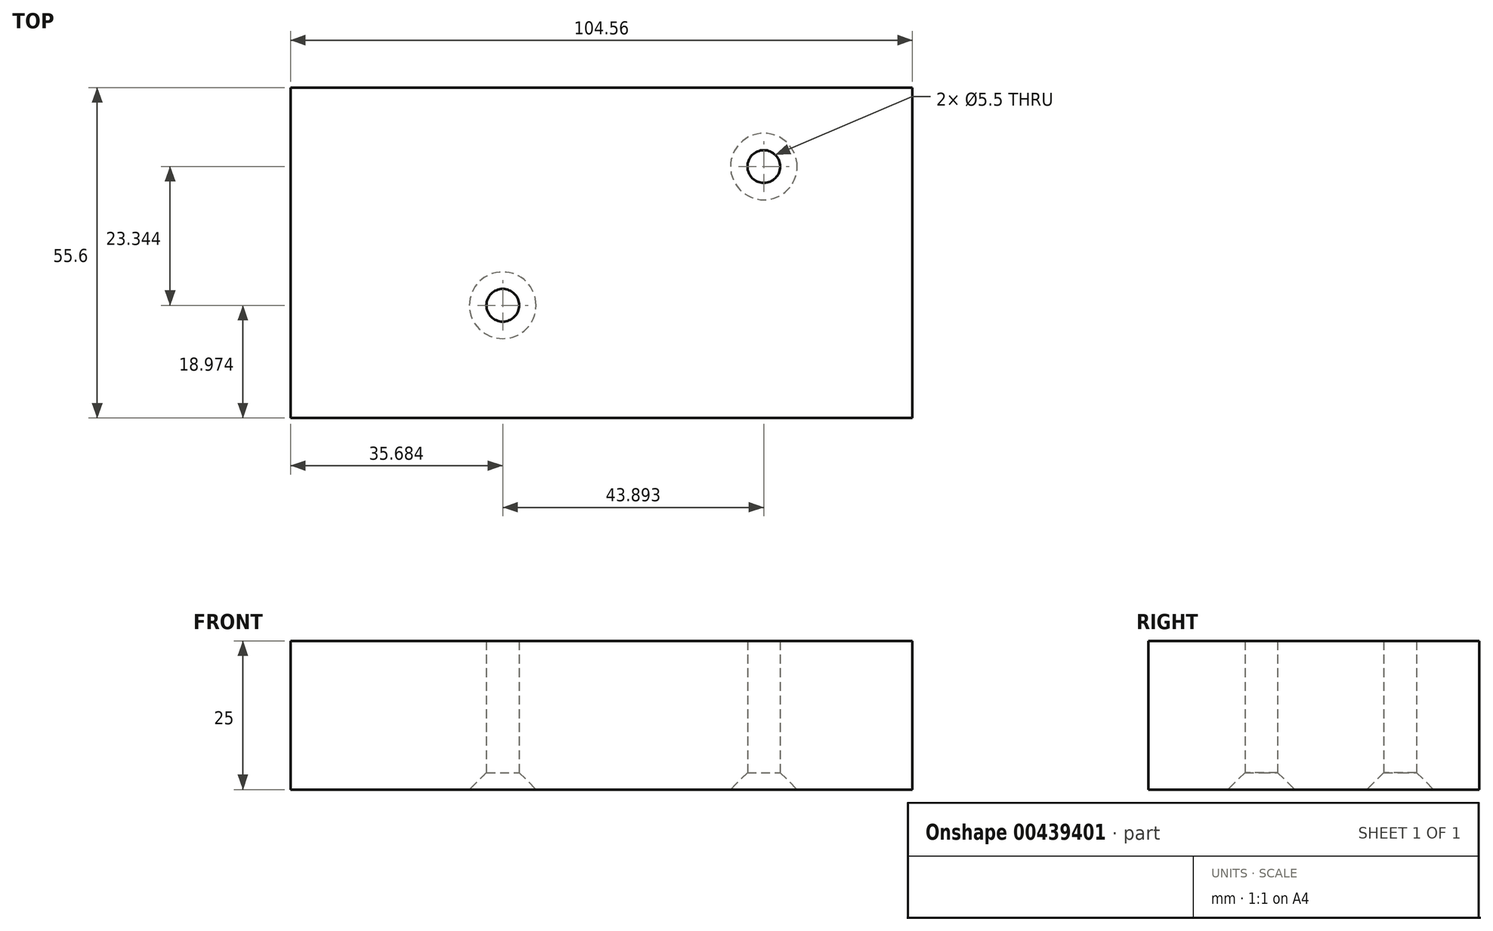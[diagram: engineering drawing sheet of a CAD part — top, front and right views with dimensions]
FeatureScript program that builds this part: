
annotation { "Feature Type Name" : "Feature", "Feature Type Description" : "" }
export const myFeature = defineFeature(function(context is Context, id is Id, definition is map)
    precondition{}
    {
        {
            var Q0;
            Q0=qCreatedBy(makeId("Top.planeOp"),FACE);
            var sketch = newSketch(context, id + "F0", { "sketchPlane" : qUnion([Q0])});
            skLineSegment(sketch, "E0.bottom", {"start": v(52.28, -27.8) * mm, "end": v(-52.28, -27.8) * mm});
            skLineSegment(sketch, "E0.top", {"start": v(52.28, 27.8) * mm, "end": v(-52.28, 27.8) * mm});
            skLineSegment(sketch, "E0.left", {"start": v(52.28, -27.8) * mm, "end": v(52.28, 27.8) * mm});
            skLineSegment(sketch, "E0.right", {"start": v(-52.28, -27.8) * mm, "end": v(-52.28, 27.8) * mm});
            skPoint(sketch, "E0.middle", {"position": v(0, 0) * mm});
            skLineSegment(sketch, "E1", {"start": v(-52.28, -27.8) * mm, "end": v(52.28, 27.8) * mm});
            skLineSegment(sketch, "E2", {"start": v(-52.28, 27.8) * mm, "end": v(1.9, -27.8) * mm});
            skPoint(sketch, "E3", {"position": v(-16.6, -8.83) * mm});
            skPoint(sketch, "E4", {"position": v(27.3, 14.52) * mm});
            skSolve(sketch);
        }
        {
            var Q0;
            Q0=makeQuery(id+"F0.imprint","IMPRINT",FACE,{"disambiguationData":[TD([[makeQuery(id+"F0.imprint","IMPRINT",EDGE,{"derivedFrom":sQuery(id+"F0.wireOp",EDGE,"E0.bottom")}),-1.0]])]});
            var Q1;
            {var subQ0=sQuery(id+"F0.wireOp",EDGE,"E0.right");Q1=makeQuery(id+"F0.imprint","IMPRINT",FACE,{"disambiguationData":[TD([[makeQuery(id+"F0.imprint","IMPRINT",EDGE,{"derivedFrom":subQ0}),-1.0]])]});}
            var Q2;
            {var subQ0=sQuery(id+"F0.wireOp",EDGE,"E0.top");Q2=makeQuery(id+"F0.imprint","IMPRINT",FACE,{"disambiguationData":[TD([[makeQuery(id+"F0.imprint","IMPRINT",EDGE,{"derivedFrom":subQ0}),1.0]])]});}
            var Q3;
            {var subQ0=sQuery(id+"F0.wireOp",EDGE,"E0.left");Q3=makeQuery(id+"F0.imprint","IMPRINT",FACE,{"disambiguationData":[TD([[makeQuery(id+"F0.imprint","IMPRINT",EDGE,{"derivedFrom":subQ0}),1.0]])]});}
            extrude(context, id + "F1", {"entities" : qUnion([Q0, Q1, Q2, Q3]), "depth" : 25 * mm, "offsetDistance" : 25 * mm});
        }
        {
            var Q0;
            Q0=sQuery(id+"F0.wireOp",VERTEX,"E4");
            var Q1;
            Q1=sQuery(id+"F0.wireOp",VERTEX,"E3");
            var Q2;
            Q2=makeQuery(id+"F1.opExtrude","SWEPT_BODY",BODY,{"disambiguationData":[OSD([sQuery(id+"F0.wireOp",EDGE,"E0.bottom"),sQuery(id+"F0.wireOp",EDGE,"E0.top"),sQuery(id+"F0.wireOp",EDGE,"E0.left"),sQuery(id+"F0.wireOp",EDGE,"E0.right")])]});
            hole(context, id + "F2", {"style" : HoleStyle.C_SINK, "endStyle" : HoleEndStyle.THROUGH, "oppositeDirection" : true, "standardTappedOrClearance" : lookupTablePath({ "standard" : "ISO", "fit" : "Normal", "size" : "M5", "type" : "Clearance" }), "standardBlindInLast" : lookupTablePath({ "fit" : "Standard", "standard" : "ISO", "size" : "M5", "type" : "Clearance" }), "holeDiameter" : 5.5 * mm, "cSinkDiameter" : 11.2 * mm, "cSinkAngle" : 90 * degree, "majorDiameter" : 8 * mm, "isTappedThrough" : true, "tappedDepth" : 12 * mm, "tapClearance" : 3, "locations" : qUnion([Q0, Q1]), "scope" : qUnion([Q2])});
        }
    });
